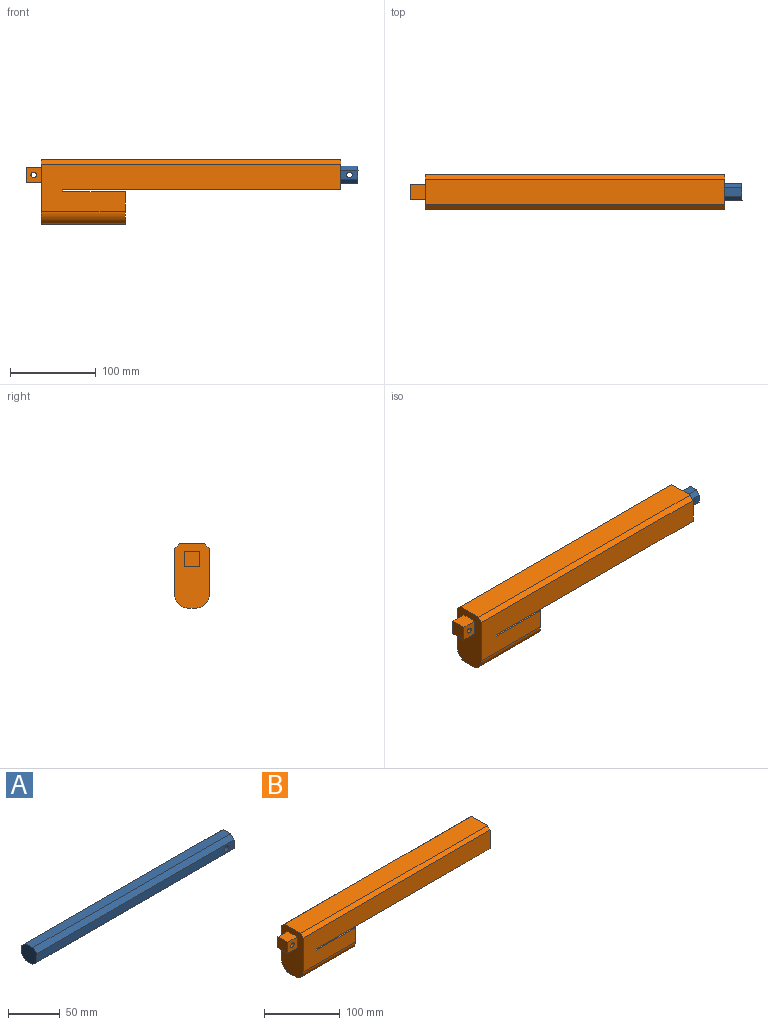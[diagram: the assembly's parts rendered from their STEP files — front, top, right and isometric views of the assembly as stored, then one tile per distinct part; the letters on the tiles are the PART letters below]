
ASSEMBLY  parts=2 mates=1
PART A: 11 faces, bbox 270x20x20 mm
  f0: plane 270x10mm, normal (0,0,1), area 2700mm2, adj f1,f4,f8,f9
  f1: plane 20x20mm, normal (-1,0,0), area 350mm2, adj f0,f2,f5,f6,f7,f8,f9,f10
  f2: plane 270x10mm, normal (0,0,-1), area 2700mm2, adj f1,f4,f7,f10
  f3: cylinder r=3.25mm len=20mm, axis (0,1,0), area 408.4mm2, adj f5,f6
  f4: plane 20x20mm, normal (1,0,0), area 350mm2, adj f0,f2,f5,f6,f7,f8,f9,f10
  f5: plane 270x10mm, normal (0,-1,0), area 2666.8mm2, adj f1,f3,f4,f7,f8
  f6: plane 270x10mm, normal (0,1,0), area 2666.8mm2, adj f1,f3,f4,f9,f10
  f7: plane 270x5mm, normal (0,-0.71,-0.71), area 1909.2mm2, adj f1,f2,f4,f5
  f8: plane 270x5mm, normal (0,-0.71,0.71), area 1909.2mm2, adj f0,f1,f4,f5
  f9: plane 270x5mm, normal (0,0.71,0.71), area 1909.2mm2, adj f0,f1,f4,f6
  f10: plane 270x5mm, normal (0,0.71,-0.71), area 1909.2mm2, adj f1,f2,f4,f6
PART B: 29 faces, bbox 368x40x75 mm
  f0: plane 18x18mm, normal (0,0,1), area 324mm2, adj f1,f4,f5,f10
  f1: plane 18x18mm, normal (-1,0,0), area 324mm2, adj f0,f3,f4,f5
  f2: cylinder r=3.25mm len=18mm, axis (0,1,0), area 367.6mm2, adj f4,f5
  f3: plane 18x18mm, normal (0,0,-1), area 324mm2, adj f1,f4,f5,f10
  f4: plane 18x18mm, normal (0,-1,0), area 290.8mm2, adj f0,f1,f2,f3,f10
  f5: plane 18x18mm, normal (0,1,0), area 290.8mm2, adj f0,f1,f2,f3,f10
  f6: plane 40x2mm, normal (1,0,0), area 80mm2, adj f7,f13,f14,f15
  f7: plane 325x40mm, normal (0,0,-1), area 13000mm2, adj f6,f8,f14,f15
  f8: plane 40x35mm, normal (1,0,0), area 1025mm2, adj f7,f9,f14,f15,f16,f17,f20,f21
  f9: plane 350x30mm, normal (0,0,1), area 10500mm2, adj f8,f10,f16,f17
  f10: plane 75x40mm, normal (-1,0,0), area 2554.4mm2, adj f0,f3,f4,f5,f9,f11,f14,f15
  f11: plane 98x10mm, normal (0,0,-1), area 980mm2, adj f10,f12,f18,f19
  f12: plane 40x38mm, normal (1,0,0), area 1423.4mm2, adj f11,f13,f14,f15,f18,f19
  f13: plane 73x40mm, normal (0,0,1), area 2920mm2, adj f6,f12,f14,f15
  f14: plane 350x55mm, normal (0,-1,0), area 12804mm2, adj f6,f7,f8,f10,f12,f13,f16,f19
  f15: plane 350x55mm, normal (0,1,0), area 12804mm2, adj f6,f7,f8,f10,f12,f13,f17,f18
  f16: plane 350x5mm, normal (0,-0.71,0.71), area 2474.9mm2, adj f8,f9,f10,f14
  f17: plane 350x5mm, normal (0,0.71,0.71), area 2474.9mm2, adj f8,f9,f10,f15
  f18: cylinder r=15mm len=98mm, axis (1,0,0), area 2309.1mm2, adj f10,f11,f12,f15
  f19: cylinder r=15mm len=98mm, axis (-1,0,0), area 2309.1mm2, adj f10,f11,f12,f14
  f20: plane 250x5mm, normal (0,0.71,0.71), area 1767.8mm2, adj f8,f21,f27,f28
  f21: plane 250x10mm, normal (0,0,1), area 2500mm2, adj f8,f20,f22,f28
  f22: plane 250x5mm, normal (0,-0.71,0.71), area 1767.8mm2, adj f8,f21,f23,f28
  f23: plane 250x10mm, normal (0,-1,0), area 2500mm2, adj f8,f22,f24,f28
  f24: plane 250x5mm, normal (0,-0.71,-0.71), area 1767.8mm2, adj f8,f23,f25,f28
  f25: plane 250x10mm, normal (0,0,-1), area 2500mm2, adj f8,f24,f26,f28
  f26: plane 250x5mm, normal (0,0.71,-0.71), area 1767.8mm2, adj f8,f25,f27,f28
  f27: plane 250x10mm, normal (0,1,0), area 2500mm2, adj f8,f20,f26,f28
  f28: plane 20x20mm, normal (1,0,0), area 350mm2, adj f20,f21,f22,f23,f24,f25,f26,f27
PLACE A t=(-500.42,-19.49,265.54)mm
PLACE B t=(-747.69,-29.49,-2.7)mm
MATE slider A.f1 <-> B.f28  axis (-1,0,0) through (-997.69,-29.49,-9.76)mm
